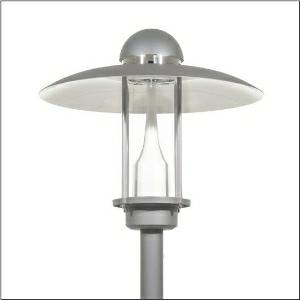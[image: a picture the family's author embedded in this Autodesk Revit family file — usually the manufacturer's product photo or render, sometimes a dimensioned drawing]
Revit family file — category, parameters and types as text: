
# Revit family: city-light_elegance_iq___st1_2a_5xa5265ef14hp_ec51
name_source: partatom
category: Lighting Fixtures
units: mm (PartAtom-declared; Revit-internal decimal feet)

## family parameters
Cut with Voids When Loaded = No
Host = Face
Light Source = No
Part Type = Normal
Room Calculation Point = No
Round Connector Dimension = Use Diameter
Shared = No

## types (1)
- --- (1 x LED, 4520 lm, 33.6 W, 3000K)
    Apparent Load = 34 VA
    CIE Flux Codes = 22 61 93 98 100
    Color Rendering = 70
    Color Temperature = 3000K
    Default Elevation = 1800 mm
    Description = City-Light Elegance iQ, mast luminaire, Module 540 iQ-SR, primary light control with 3 zone facetted reflector, of plastic, silver coated, highly specular, structured, primary optical cover: cover, of PMMA, transparent, light distribution: ST1.2a, light emission: direct distribution, primary light characteristic: asymmetric, installation type: post-top, LED, High Power LED, rated luminous flux: 4.520lm, luminous efficacy: 135lm/W, light colour: 730, colour temperature: 3000K, control gear: iQ Street-Remote, control: pre-setting: logarithmic dimming characteristic, Street-Remote, Auto-Match, Temp-Guard, Lumen-Switch, Night-Set, Smart-Wire, Light-Fading, Desk-Remote (wireless, voltage-free reading and setting of iQ features in the workshop via application-optimized NFC function/RFID function), optimised constant luminous flux control (CLO 2.0), with terminal, 6-pole, max. 2.5mm², mains connection: 230..240V, AC, 50/60Hz, start of lifetime: 34W, end of service life: 36W, reduction: 15W, luminaire housing, upper part, of aluminium, coated, Siteco® metallic grey (DB 702S), diameter: 750mm, height: 675mm, spigot size: d x l = 76 x 70mm (post-top) | with reducer (optional accessory) 60 x 70mm, mounting height: 3..5m, post-top mast mounting element, of diecast aluminium, coated, Siteco® metallic grey (DB 702S), Module 540 iQ-SR, traffic white (RAL 9016), equipment: Power, protection rating (complete): IP65, insulation class (complete): insulation class II (safety insulation), certification: CE, ENEC, VDE, packaging unit: 1 piece

Light Distribution: ST1.2a
    Height = 675 mm
    Lamp = 1 x LED
    Lamp Light Flux = 4520 lm
    Lamp Power = 33.6 W
    Lamp count = 1
    Length = 750 mm
    Luminous efficacy = 135 lm/W
    Manufacturer = Siteco
    ModVariant = No
    Model = 5XA5265EF14HP
    Number of Poles = 1
    OnlyDefault = Yes
    Power Factor = 1
    Product Name = City-Light Elegance iQ | ST1.2a
    Product group = mast luminaire | pylon top
    ProductGroupID = 6100
    Protection Class = Protection class II
    Protection Degree = IP 65
    RLX_Detail_Level = 1
    RLX_Emergency_Light_Flux = 0 lm
    RLX_Emergency_Type = 0
    RLX_Emergency_Type_DB = No
    RlxData = <blob elided: 36637 chars, md5=beae0a2d>
    Socket = socket
    Standby Power = 0 W
    System Light Flux = 4520 lm
    System Power = 34 W
    Type Comments = factory setting: luminous flux: 100 % | dim-lin: 254 | 695 mA
    Type Image = l_1006912.jpg
    URL = http://relux.com
    VarID = @adj_214351
    Voltage = 0 V
    Weight = 0.00 kg
    Width = 0 mm  [stored 0 ft]

note: [stored X ft] marks values corroborated as IEEE doubles in the binary element streams (Revit-internal decimal feet)

## geometry (parser evidence)
native form markers: Blend x4, Sweep x10
no freeform markers — native parametric forms only
